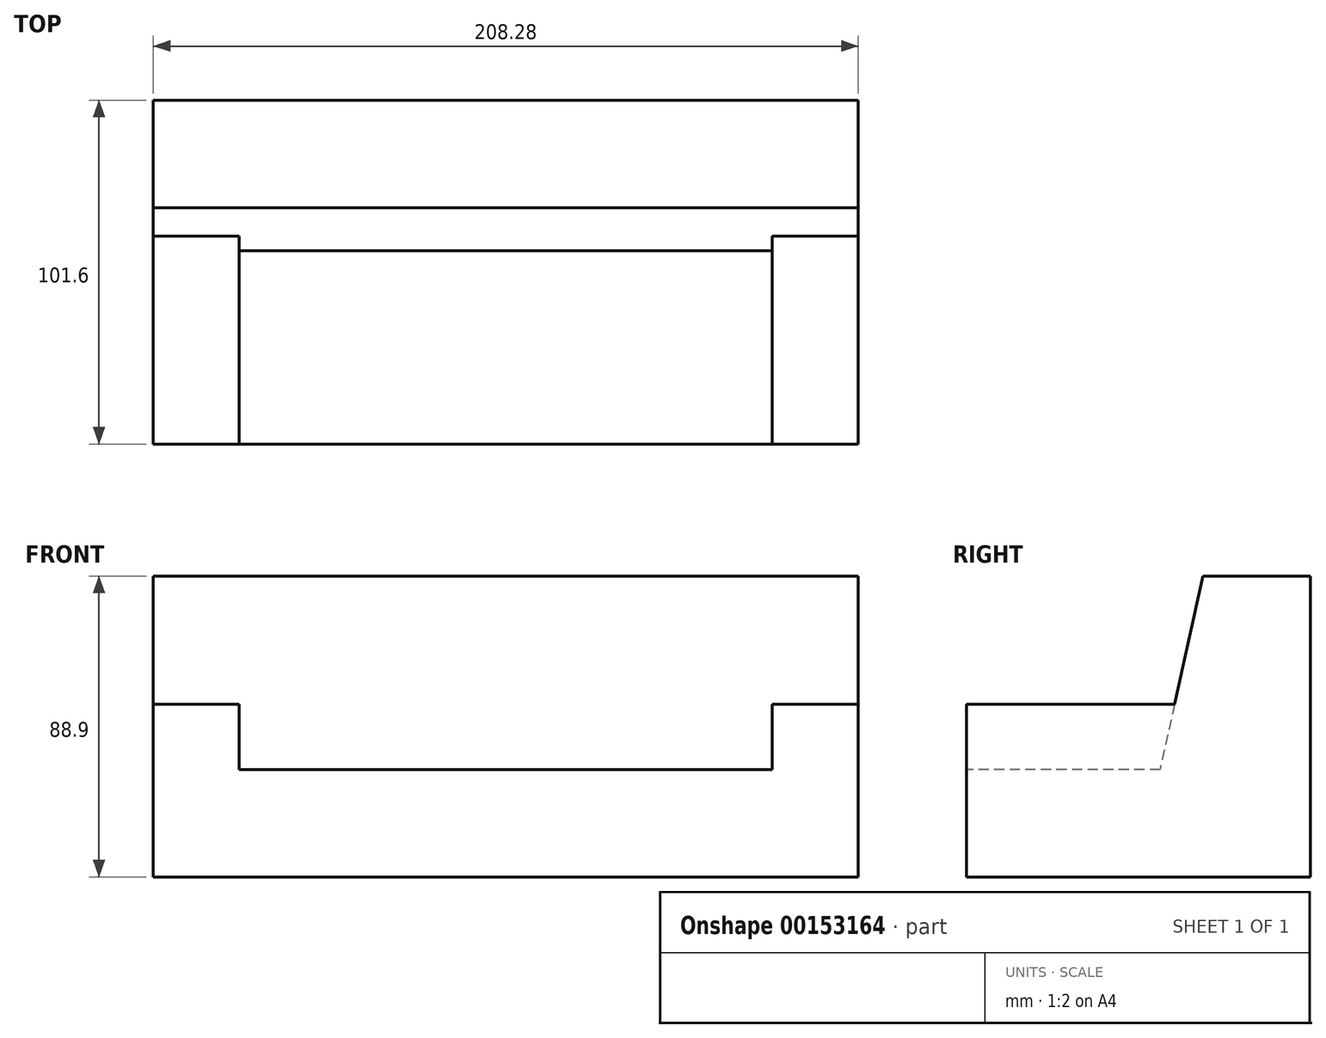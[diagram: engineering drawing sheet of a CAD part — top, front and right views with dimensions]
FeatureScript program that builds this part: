
annotation { "Feature Type Name" : "Feature", "Feature Type Description" : "" }
export const myFeature = defineFeature(function(context is Context, id is Id, definition is map)
    precondition{}
    {
        {
            var Q0;
            Q0=qCreatedBy(makeId("Right.planeOp"),FACE);
            var sketch = newSketch(context, id + "F0", { "sketchPlane" : qUnion([Q0])});
            skLineSegment(sketch, "E0", {"start": v(0, 0) * mm, "end": v(0, 88.9) * mm});
            skLineSegment(sketch, "E1", {"start": v(0, 88.9) * mm, "end": v(-31.75, 88.9) * mm});
            skLineSegment(sketch, "E2", {"start": v(-31.75, 88.9) * mm, "end": v(-44.45, 31.75) * mm});
            skLineSegment(sketch, "E3", {"start": v(-44.45, 31.75) * mm, "end": v(-101.6, 31.75) * mm});
            skLineSegment(sketch, "E4", {"start": v(-101.6, 31.75) * mm, "end": v(-101.6, 0) * mm});
            skLineSegment(sketch, "E5", {"start": v(-101.6, 0) * mm, "end": v(0, 0) * mm});
            skSolve(sketch);
        }
        {
            var Q0;
            Q0 = qSketchRegion(id + "F0", true);
            extrude(context, id + "F1", {"entities" : qUnion([Q0]), "endBound" : BoundingType.SYMMETRIC, "depth" : 208.28 * mm});
        }
        {
            var Q0;
            Q0=makeQuery(id+"F1.opExtrude","CAP_FACE",FACE,{"disambiguationData":[OSD([sQuery(id+"F0.wireOp",EDGE,"E0"),sQuery(id+"F0.wireOp",EDGE,"E1"),sQuery(id+"F0.wireOp",EDGE,"E2"),sQuery(id+"F0.wireOp",EDGE,"E3"),sQuery(id+"F0.wireOp",EDGE,"E4"),sQuery(id+"F0.wireOp",EDGE,"E5")])],"isStart":false});
            var sketch = newSketch(context, id + "F2", { "sketchPlane" : qUnion([Q0])});
            skLineSegment(sketch, "E6", {"start": v(-101.6, 0) * mm, "end": v(-101.6, 50.96) * mm});
            skLineSegment(sketch, "E7", {"start": v(-101.6, 50.96) * mm, "end": v(0, 50.96) * mm});
            skLineSegment(sketch, "E8", {"start": v(0, 50.96) * mm, "end": v(0, 0) * mm});
            skLineSegment(sketch, "E9", {"start": v(0, 0) * mm, "end": v(-101.6, 0) * mm});
            skSolve(sketch);
        }
        {
            var Q0;
            Q0 = qSketchRegion(id + "F2", true);
            extrude(context, id + "F3", {"entities" : qUnion([Q0]), "operationType" : NewBodyOperationType.ADD, "oppositeDirection" : true, "depth" : 25.4 * mm});
        }
        {
            var Q0;
            Q0=makeQuery(id+"F1.opExtrude","SWEPT_BODY",BODY,{"disambiguationData":[OSD([sQuery(id+"F0.wireOp",EDGE,"E0"),sQuery(id+"F0.wireOp",EDGE,"E1"),sQuery(id+"F0.wireOp",EDGE,"E2"),sQuery(id+"F0.wireOp",EDGE,"E3"),sQuery(id+"F0.wireOp",EDGE,"E4"),sQuery(id+"F0.wireOp",EDGE,"E5")])]});
            var Q1;
            Q1=qCreatedBy(makeId("Right.planeOp"),FACE);
            mirror(context, id + "F4", {"operationType" : NewBodyOperationType.ADD, "entities" : qUnion([Q0]), "mirrorPlane" : qUnion([Q1])});
        }
    });
